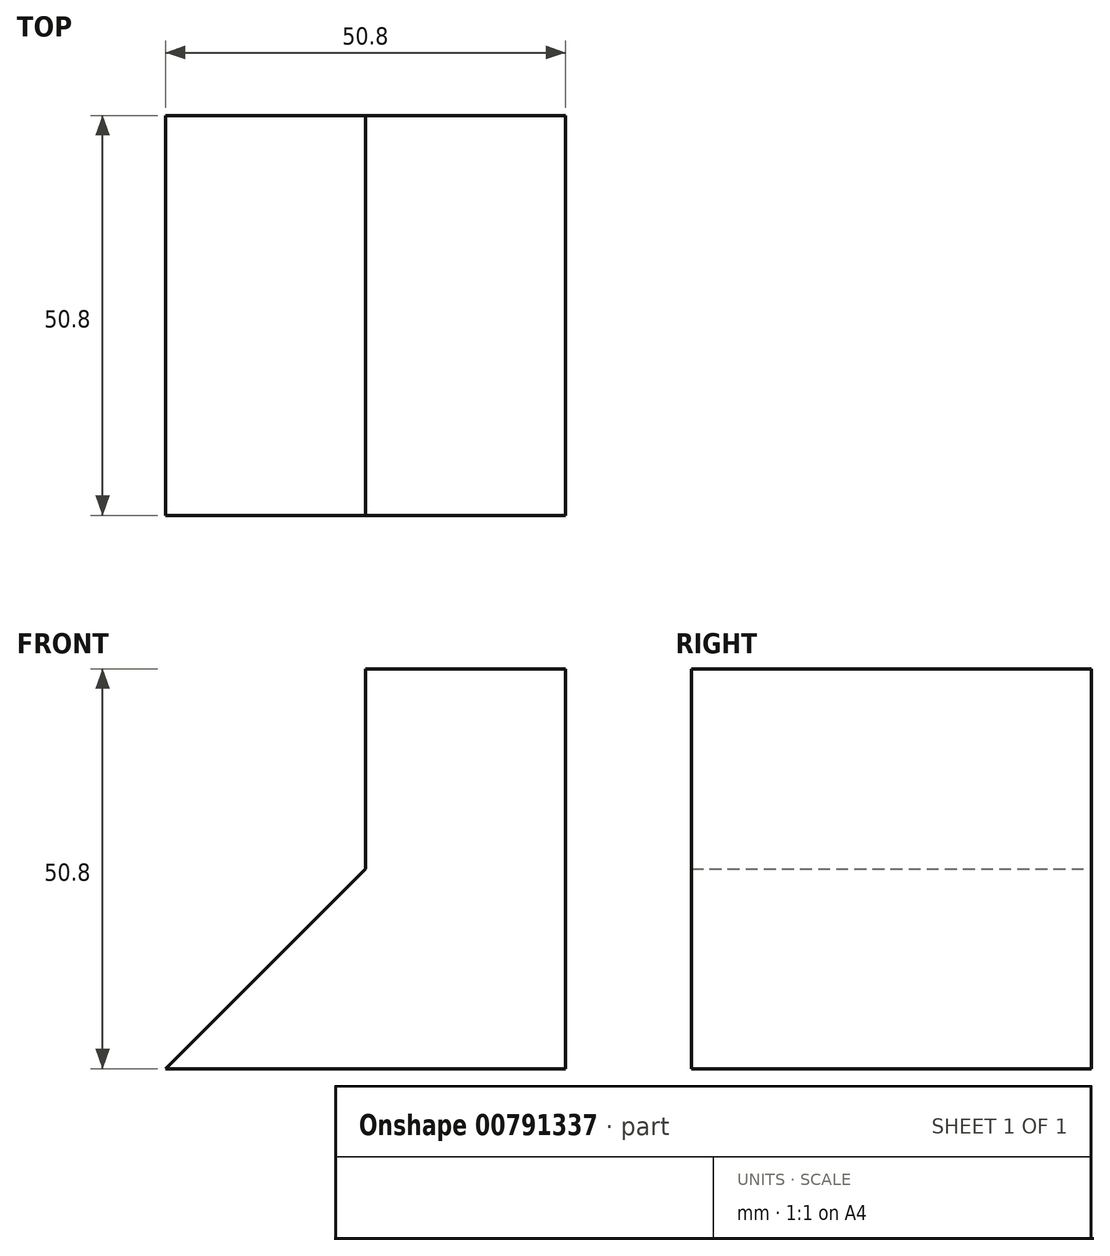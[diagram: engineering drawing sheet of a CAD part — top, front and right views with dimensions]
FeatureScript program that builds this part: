
annotation { "Feature Type Name" : "Feature", "Feature Type Description" : "" }
export const myFeature = defineFeature(function(context is Context, id is Id, definition is map)
    precondition{}
    {
        {
            var Q0;
            Q0=qCreatedBy(makeId("Front.planeOp"),FACE);
            var sketch = newSketch(context, id + "F0", { "sketchPlane" : qUnion([Q0])});
            skLineSegment(sketch, "E0", {"start": v(0, 0) * mm, "end": v(50.8, 0) * mm});
            skLineSegment(sketch, "E1", {"start": v(50.8, 0) * mm, "end": v(50.8, 50.8) * mm});
            skLineSegment(sketch, "E2", {"start": v(50.8, 50.8) * mm, "end": v(25.4, 50.8) * mm});
            skLineSegment(sketch, "E3", {"start": v(25.4, 50.8) * mm, "end": v(25.4, 25.4) * mm});
            skLineSegment(sketch, "E4", {"start": v(25.4, 25.4) * mm, "end": v(0, 0) * mm});
            skSolve(sketch);
        }
        {
            var Q0;
            Q0=qSketchRegion(id+"F0",true);
            extrude(context, id + "F1", {"entities" : qUnion([Q0]), "depth" : 50.8 * mm, "offsetDistance" : 25.4 * mm});
        }
    });
